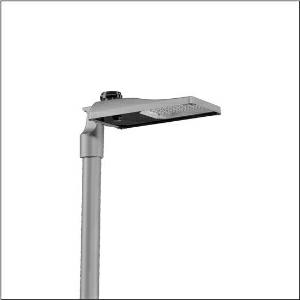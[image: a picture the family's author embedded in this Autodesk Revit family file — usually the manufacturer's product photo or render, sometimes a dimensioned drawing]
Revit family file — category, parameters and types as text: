
# Revit family: streetlight_sl_31_mini___st1_0a_5xh6d35m08ga_0c89
name_source: partatom
category: Lighting Fixtures
units: mm (PartAtom-declared; Revit-internal decimal feet)

## family parameters
Cut with Voids When Loaded = No
Host = Face
Light Source = No
Part Type = Normal
Room Calculation Point = No
Round Connector Dimension = Use Diameter
Shared = No

## types (1)
- --- (1 x LED, 5880 lm, 39.3 W, 3000K)
    Apparent Load = 39 VA
    CIE Flux Codes = 37 72 97 100 100
    Color Rendering = 70
    Color Temperature = 3000K
    Default Elevation = 1800 mm
    Description = Streetlight SL 31 mini NEMA (7pin), Desk-Remote mast luminaire for post-top, side-entry; light control with lens of PMMA; light distribution: ST1.0a, direct asymmetric distribution, for standard-compliant lighting for roads and squares; LED: luminous flux: 5.880lm, light colour: 730, colour temperature: 3000K; luminous efficacy: 149,6lm/W; control: pre-setting: linear dimming characteristic, flexible luminous flux parameterisation, time-dependent luminous flux control, constant luminous flux control, intelligent temperature release in ECG and LED module, overheat protection; luminaire housing, of diecast aluminium, Siteco® metallic grey (DB 702S), corrosivity category C5 high according to DIN EN ISO 12944; cover of toughened safety glass, transparent, opened without tools; mast flange of diecast aluminium, Siteco® metallic grey (DB 702S), spigot size: 76/60mm, mast flange included unmounted; with cable H07RN-F 3x 1.5mm², cable length: 6,5m, connection cable pre-assembled; mains connection: 220..240V, AC, 50/60Hz; power consumption (at start of service life): 39,3W / (at end of service life): 40,7W / (with reduced operation 50%): 18,1W; protection rating (complete): IP66; insulation class (complete): insulation class I (protective earthing); impact resistance: IK09; certification: CE, ENEC, ENEC+, VDE, UKCA; permissible operating ambient temperature for outdoor applications: -40..+50°C; packaging unit: 1 piece

Light Distribution: ST1.0a
    Height = 76 mm
    Lamp = 1 x LED
    Lamp Light Flux = 5880 lm
    Lamp Power = 39.3 W
    Lamp count = 1
    Length = 547 mm
    Luminous efficacy = 150 lm/W
    Manufacturer = Siteco
    ModVariant = No
    Model = 5XH6D35M08GA
    Number of Poles = 1
    OnlyDefault = Yes
    Power Factor = 1
    Product Name = Streetlight SL 31 mini | ST1.0a
    Product group = mast luminaire | pylon top
    ProductGroupID = 6100
    Protection Class = Protection class I
    Protection Degree = IP 66
    RLX_Detail_Level = 1
    RLX_Emergency_Light_Flux = 0 lm
    RLX_Emergency_Type = 0
    RLX_Emergency_Type_DB = No
    RlxData = <blob elided: 40353 chars, md5=dccfff64>
    Socket = socket
    Standby Power = 0 W
    System Light Flux = 5880 lm
    System Power = 39 W
    Type Comments = factory setting: luminous flux: 100 % | dim-lin: 254 | 798 mA
    Type Image = l_1300324.jpg
    URL = http://relux.com
    VarID = @adj_074071
    Voltage = 0 V
    Weight = 0.00 kg
    Width = 265 mm

## geometry (parser evidence)
native form markers: Blend x4, Sweep x9
no freeform markers — native parametric forms only
